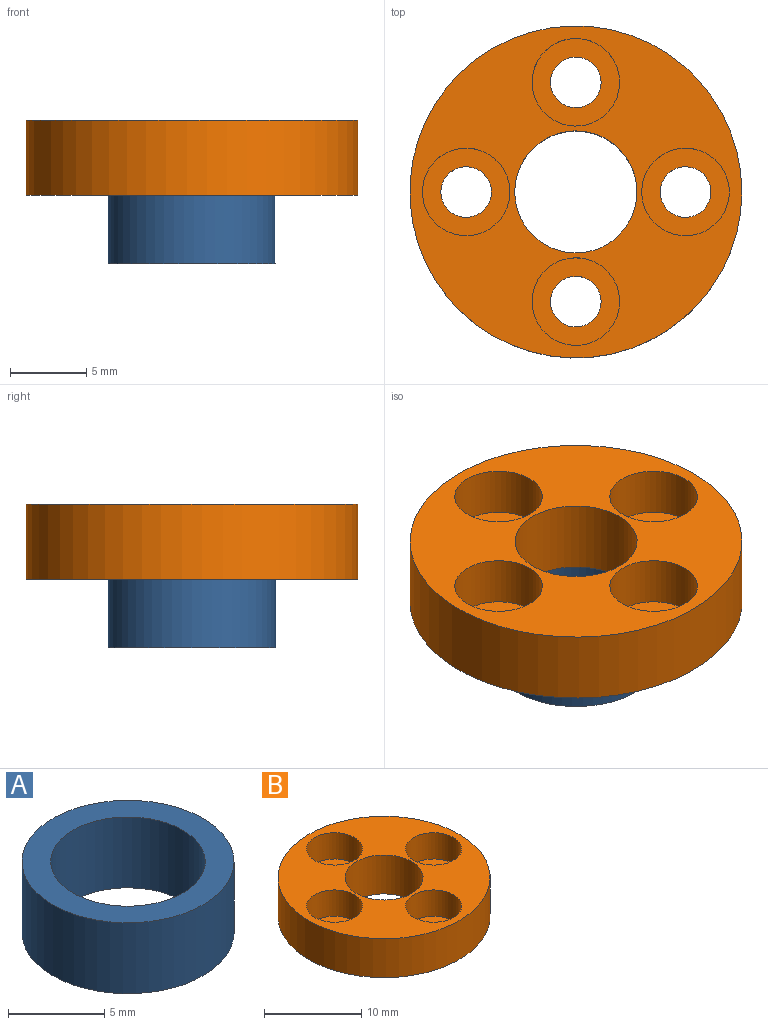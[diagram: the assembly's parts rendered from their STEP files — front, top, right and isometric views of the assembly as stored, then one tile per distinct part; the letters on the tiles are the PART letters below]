
ASSEMBLY  parts=2 mates=1
PART A: 4 faces, bbox 11x11x4.5 mm
  f0: cylinder r=4.01mm len=8.02mm, axis (0,0,1), area 113.3mm2, adj f2,f3
  f1: cylinder r=5.5mm len=11mm, axis (0,0,1), area 155.5mm2, adj f2,f3
  f2: plane 11x11mm, normal (0,0,-1), area 44.6mm2, adj f0,f1
  f3: plane 11x11mm, normal (0,0,1), area 44.6mm2, adj f0,f1
PART B: 16 faces, bbox 21.8x21.8x4.9 mm
  f0: cylinder r=1.66mm len=3.32mm, axis (0,0,1), area 16.7mm2, adj f6,f9
  f1: cylinder r=1.66mm len=3.32mm, axis (0,0,1), area 16.7mm2, adj f6,f13
  f2: cylinder r=1.66mm len=3.32mm, axis (0,0,1), area 16.7mm2, adj f6,f15
  f3: cylinder r=1.66mm len=3.32mm, axis (0,0,1), area 16.7mm2, adj f6,f11
  f4: cylinder r=10.9mm len=21.8mm, axis (0,0,1), area 335.6mm2, adj f6,f7
  f5: cylinder r=4.01mm len=8.02mm, axis (0,0,1), area 123.4mm2, adj f6,f7
  f6: plane 21.8x21.8mm, normal (0,0,-1), area 288.2mm2, adj f0,f1,f2,f3,f4,f5
  f7: plane 21.8x21.8mm, normal (0,0,1), area 218.9mm2, adj f4,f5,f8,f10,f12,f14
  f8: cylinder r=2.88mm len=5.75mm, axis (0,0,1), area 59.6mm2, adj f7,f9
  f9: plane 5.75x5.75mm, normal (0,0,1), area 17.3mm2, adj f0,f8
  f10: cylinder r=2.88mm len=5.75mm, axis (0,0,1), area 59.6mm2, adj f7,f11
  f11: plane 5.75x5.75mm, normal (0,0,1), area 17.3mm2, adj f3,f10
  f12: cylinder r=2.88mm len=5.75mm, axis (0,0,1), area 59.6mm2, adj f7,f13
  f13: plane 5.75x5.75mm, normal (0,0,1), area 17.3mm2, adj f1,f12
  f14: cylinder r=2.88mm len=5.75mm, axis (0,0,1), area 59.6mm2, adj f7,f15
  f15: plane 5.75x5.75mm, normal (0,0,1), area 17.3mm2, adj f2,f14
PLACE A t=(-4.04,-1.45,1.78)mm
PLACE B t=(-4.04,-1.45,1.78)mm
MATE fastened A.f0 <-> B.f5  axis (0,0,1) through (-4.04,-1.45,-3.12)mm
